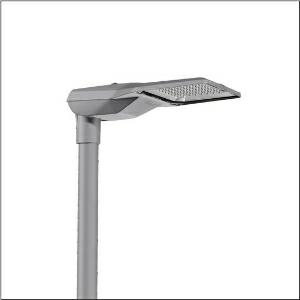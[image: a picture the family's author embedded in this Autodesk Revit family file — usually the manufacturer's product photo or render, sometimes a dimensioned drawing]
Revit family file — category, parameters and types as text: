
# Revit family: streetlight_sl_21_midi___stw1_0a_5xe3e33s08nb_8a4c
name_source: partatom
category: Lighting Fixtures
units: mm (PartAtom-declared; Revit-internal decimal feet)

## family parameters
Cut with Voids When Loaded = No
Host = Face
Light Source = No
Part Type = Normal
Room Calculation Point = No
Round Connector Dimension = Use Diameter
Shared = No

## types (1)
- --- (1 x LED, 22700 lm, 151.2 W, 3000K)
    Apparent Load = 151 VA
    CIE Flux Codes = 39 75 98 100 100
    Color Rendering = 70
    Color Temperature = 3000K
    Default Elevation = 1800 mm
    Description = Streetlight SL 21 midi, mast luminaire, primary light control with lens, of PMMA, primary optical cover: cover, of toughened safety glass, transparent, light distribution: STW1.0a, light emission: direct distribution, primary light characteristic: asymmetric, installation type: side-entry, post-top, LED, High Power LED, rated luminous flux: 22.700lm, luminous efficacy: 150lm/W, light colour: 730, colour temperature: 3000K, control gear: D4i, control: overheat protection, constant luminous flux control, time-dependent luminous flux control, flexible luminous flux parameterisation, pre-setting: logarithmic dimming characteristic, mains connection: 230..240V, AC, 50/60Hz, start of lifetime: 151W, end of service life: 157W, reduction: 70W, luminaire housing, of diecast aluminium, powder-coated, Siteco® metallic grey (DB 702S), corrosivity category C5 mid according to DIN EN ISO 12944, please order mast flange separately, inclination adjustable: 0°, 5°, 10°, 15°, sealing non-destructively replaceable, multi-level sealing system, length: 644mm, width: 335mm, height: 110mm, mast flange for spigot size: 42mm (side-entry): 5XC10008XM4, 60/48mm (side-entry/post-top): 5XC10108XM2, 76/60mm (side-entry/post-top): 5XC10108XM1, mounting height: 4..8m, Smart Interface above, protection rating (complete): IP66, insulation class (complete): insulation class II (safety insulation), certification: CE, ENEC, ENEC+, VDE, impact resistance: IK10, permissible operating ambient temperature for outdoor applications: -40..+50°C, standard-compliant lighting for roads and squares, packaging unit: 1 piece

Light Distribution: STW1.0a
    Height = 111 mm
    Lamp = 1 x LED
    Lamp Light Flux = 22700 lm
    Lamp Power = 151.2 W
    Lamp count = 1
    Length = 644 mm
    Luminous efficacy = 150 lm/W
    Manufacturer = Siteco
    ModVariant = No
    Model = 5XE3E33S08NB
    Number of Poles = 1
    OnlyDefault = Yes
    Power Factor = 1
    Product Name = Streetlight SL 21 midi | STW1.0a
    Product group = mast luminaire | pylon top
    ProductGroupID = 6100
    Protection Class = Protection class II
    Protection Degree = IP 66
    RLX_Detail_Level = 1
    RLX_Emergency_Light_Flux = 0 lm
    RLX_Emergency_Type = 0
    RLX_Emergency_Type_DB = No
    RlxData = <blob elided: 26993 chars, md5=77dfef5e>
    Socket = socket
    Standby Power = 0 W
    System Light Flux = 22700 lm
    System Power = 151 W
    Type Comments = factory setting: luminous flux: 100 % | dim-lin: 254 | 802 mA
    Type Image = l_1004302.jpg
    URL = http://relux.com
    VarID = @adj_191151
    Voltage = 0 V
    Weight = 0.00 kg
    Width = 336 mm

## geometry (parser evidence)
native form markers: Blend x4, Sweep x10
no freeform markers — native parametric forms only
